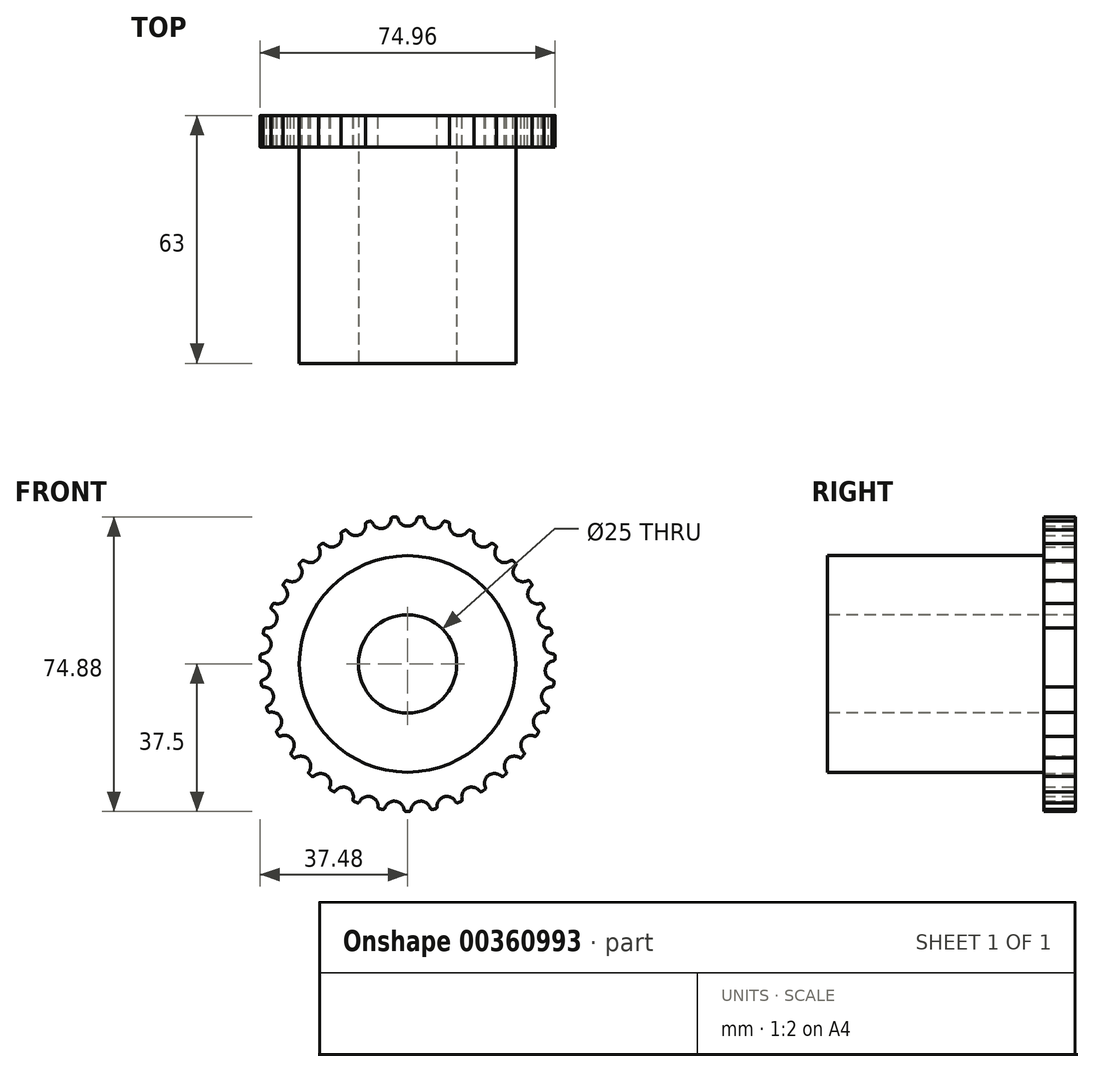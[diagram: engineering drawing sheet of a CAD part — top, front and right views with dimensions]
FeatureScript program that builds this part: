
annotation { "Feature Type Name" : "Feature", "Feature Type Description" : "" }
export const myFeature = defineFeature(function(context is Context, id is Id, definition is map)
    precondition{}
    {
        {
            var Q0;
            Q0=qCreatedBy(makeId("Front.planeOp"),FACE);
            var sketch = newSketch(context, id + "F0", { "sketchPlane" : qUnion([Q0])});
            skCircle(sketch, "E0", {"center": v(0, 0) * mm, "radius": 37.5 * mm});
            skSolve(sketch);
        }
        {
            var Q0;
            Q0=makeQuery(id+"F0.imprint","IMPRINT",FACE,{"disambiguationData":[TD([[makeQuery(id+"F0.imprint","IMPRINT",EDGE,{"derivedFrom":sQuery(id+"F0.wireOp",EDGE,"E0")}),1.0]])]});
            extrude(context, id + "F1", {"entities" : qUnion([Q0]), "endBound" : BoundingType.SYMMETRIC, "oppositeDirection" : true, "depth" : 8 * mm});
        }
        {
            var Q0;
            Q0=makeQuery(id+"F1.opExtrude","CAP_FACE",FACE,{"disambiguationData":[OSD([sQuery(id+"F0.wireOp",EDGE,"E0")])],"isStart":false});
            var sketch = newSketch(context, id + "F2", { "sketchPlane" : qUnion([Q0])});
            skArc(sketch, "E1", {"start": v(-2.45, 36.99) * mm, "mid": v(0, 35) * mm, "end": v(2.45, 36.99) * mm});
            skLineSegment(sketch, "E2", {"start": v(0, 0) * mm, "end": v(0, 37.5) * mm, "construction": true});
            skPoint(sketch, "E3.visualSharp", {"position": v(2.5, 37.42) * mm});
            skArc(sketch, "E3.filletArc", {"start": v(2.98, 37.38) * mm, "mid": v(2.64, 37.28) * mm, "end": v(2.45, 36.99) * mm});
            skPoint(sketch, "E4.visualSharp", {"position": v(-2.5, 37.42) * mm});
            skArc(sketch, "E4.filletArc", {"start": v(-2.45, 36.99) * mm, "mid": v(-2.64, 37.28) * mm, "end": v(-2.98, 37.38) * mm});
            skLineSegment(sketch, "E5", {"start": v(2.98, 37.38) * mm, "end": v(1.5, 39.5) * mm});
            skLineSegment(sketch, "E6", {"start": v(1.5, 39.5) * mm, "end": v(-1.5, 39.5) * mm});
            skLineSegment(sketch, "E7", {"start": v(-1.5, 39.5) * mm, "end": v(-2.98, 37.38) * mm});
            skLineSegment(sketch, "E8.1.0", {"start": v(-3.75, 37.31) * mm, "end": v(-5.58, 39.13) * mm});
            skLineSegment(sketch, "E8.1.1", {"start": v(-5.58, 39.13) * mm, "end": v(-8.53, 38.6) * mm});
            skLineSegment(sketch, "E8.1.2", {"start": v(-8.53, 38.6) * mm, "end": v(-9.6, 36.25) * mm});
            skArc(sketch, "E8.1.3", {"start": v(-9.01, 35.95) * mm, "mid": v(-9.25, 36.21) * mm, "end": v(-9.6, 36.25) * mm});
            skArc(sketch, "E8.1.4", {"start": v(-9.01, 35.95) * mm, "mid": v(-6.25, 34.44) * mm, "end": v(-4.2, 36.83) * mm});
            skArc(sketch, "E8.1.5", {"start": v(-3.75, 37.31) * mm, "mid": v(-4.06, 37.16) * mm, "end": v(-4.2, 36.83) * mm});
            skLineSegment(sketch, "E8.2.0", {"start": v(-10.35, 36.04) * mm, "end": v(-12.47, 37.5) * mm});
            skLineSegment(sketch, "E8.2.1", {"start": v(-12.47, 37.5) * mm, "end": v(-15.28, 36.45) * mm});
            skLineSegment(sketch, "E8.2.2", {"start": v(-15.28, 36.45) * mm, "end": v(-15.92, 33.95) * mm});
            skArc(sketch, "E8.2.3", {"start": v(-15.29, 33.77) * mm, "mid": v(-15.57, 33.98) * mm, "end": v(-15.92, 33.95) * mm});
            skArc(sketch, "E8.2.4", {"start": v(-15.29, 33.77) * mm, "mid": v(-12.3, 32.77) * mm, "end": v(-10.7, 35.49) * mm});
            skArc(sketch, "E8.2.5", {"start": v(-10.35, 36.04) * mm, "mid": v(-10.63, 35.83) * mm, "end": v(-10.7, 35.49) * mm});
            skLineSegment(sketch, "E8.3.0", {"start": v(-16.62, 33.62) * mm, "end": v(-18.97, 34.68) * mm});
            skLineSegment(sketch, "E8.3.1", {"start": v(-18.97, 34.68) * mm, "end": v(-21.55, 33.14) * mm});
            skLineSegment(sketch, "E8.3.2", {"start": v(-21.55, 33.14) * mm, "end": v(-21.73, 30.56) * mm});
            skArc(sketch, "E8.3.3", {"start": v(-21.07, 30.5) * mm, "mid": v(-21.39, 30.65) * mm, "end": v(-21.73, 30.56) * mm});
            skArc(sketch, "E8.3.4", {"start": v(-21.07, 30.5) * mm, "mid": v(-17.95, 30.05) * mm, "end": v(-16.87, 33) * mm});
            skArc(sketch, "E8.3.5", {"start": v(-16.62, 33.62) * mm, "mid": v(-16.86, 33.36) * mm, "end": v(-16.87, 33) * mm});
            skLineSegment(sketch, "E8.4.0", {"start": v(-22.35, 30.1) * mm, "end": v(-24.86, 30.73) * mm});
            skLineSegment(sketch, "E8.4.1", {"start": v(-24.86, 30.73) * mm, "end": v(-27.12, 28.76) * mm});
            skLineSegment(sketch, "E8.4.2", {"start": v(-27.12, 28.76) * mm, "end": v(-26.84, 26.2) * mm});
            skArc(sketch, "E8.4.3", {"start": v(-26.18, 26.24) * mm, "mid": v(-26.52, 26.34) * mm, "end": v(-26.84, 26.2) * mm});
            skArc(sketch, "E8.4.4", {"start": v(-26.18, 26.24) * mm, "mid": v(-23.03, 26.36) * mm, "end": v(-22.5, 29.46) * mm});
            skArc(sketch, "E8.4.5", {"start": v(-22.35, 30.1) * mm, "mid": v(-22.54, 29.81) * mm, "end": v(-22.5, 29.46) * mm});
            skLineSegment(sketch, "E8.5.0", {"start": v(-27.37, 25.63) * mm, "end": v(-29.95, 25.8) * mm});
            skLineSegment(sketch, "E8.5.1", {"start": v(-29.95, 25.8) * mm, "end": v(-31.82, 23.46) * mm});
            skLineSegment(sketch, "E8.5.2", {"start": v(-31.82, 23.46) * mm, "end": v(-31.08, 20.98) * mm});
            skArc(sketch, "E8.5.3", {"start": v(-30.44, 21.15) * mm, "mid": v(-30.8, 21.18) * mm, "end": v(-31.08, 20.98) * mm});
            skArc(sketch, "E8.5.4", {"start": v(-30.44, 21.15) * mm, "mid": v(-27.36, 21.82) * mm, "end": v(-27.4, 24.97) * mm});
            skArc(sketch, "E8.5.5", {"start": v(-27.37, 25.63) * mm, "mid": v(-27.5, 25.3) * mm, "end": v(-27.4, 24.97) * mm});
            skLineSegment(sketch, "E8.6.0", {"start": v(-31.5, 20.33) * mm, "end": v(-34.07, 20.04) * mm});
            skLineSegment(sketch, "E8.6.1", {"start": v(-34.07, 20.04) * mm, "end": v(-35.5, 17.4) * mm});
            skLineSegment(sketch, "E8.6.2", {"start": v(-35.5, 17.4) * mm, "end": v(-34.33, 15.1) * mm});
            skArc(sketch, "E8.6.3", {"start": v(-33.73, 15.37) * mm, "mid": v(-34.08, 15.35) * mm, "end": v(-34.33, 15.1) * mm});
            skArc(sketch, "E8.6.4", {"start": v(-33.73, 15.37) * mm, "mid": v(-30.82, 16.59) * mm, "end": v(-31.41, 19.68) * mm});
            skArc(sketch, "E8.6.5", {"start": v(-31.5, 20.33) * mm, "mid": v(-31.58, 19.99) * mm, "end": v(-31.41, 19.68) * mm});
            skLineSegment(sketch, "E8.7.0", {"start": v(-34.63, 14.38) * mm, "end": v(-37.1, 13.63) * mm});
            skLineSegment(sketch, "E8.7.1", {"start": v(-37.1, 13.63) * mm, "end": v(-38.03, 10.78) * mm});
            skLineSegment(sketch, "E8.7.2", {"start": v(-38.03, 10.78) * mm, "end": v(-36.47, 8.72) * mm});
            skArc(sketch, "E8.7.3", {"start": v(-35.93, 9.1) * mm, "mid": v(-36.27, 9.01) * mm, "end": v(-36.47, 8.72) * mm});
            skArc(sketch, "E8.7.4", {"start": v(-35.93, 9.1) * mm, "mid": v(-33.29, 10.82) * mm, "end": v(-34.42, 13.76) * mm});
            skArc(sketch, "E8.7.5", {"start": v(-34.63, 14.38) * mm, "mid": v(-34.64, 14.03) * mm, "end": v(-34.42, 13.76) * mm});
            skLineSegment(sketch, "E8.8.0", {"start": v(-36.64, 7.97) * mm, "end": v(-38.94, 6.79) * mm});
            skLineSegment(sketch, "E8.8.1", {"start": v(-38.94, 6.79) * mm, "end": v(-39.34, 3.82) * mm});
            skLineSegment(sketch, "E8.8.2", {"start": v(-39.34, 3.82) * mm, "end": v(-37.44, 2.07) * mm});
            skArc(sketch, "E8.8.3", {"start": v(-36.98, 2.54) * mm, "mid": v(-37.3, 2.4) * mm, "end": v(-37.44, 2.07) * mm});
            skArc(sketch, "E8.8.4", {"start": v(-36.98, 2.54) * mm, "mid": v(-34.68, 4.7) * mm, "end": v(-36.32, 7.39) * mm});
            skArc(sketch, "E8.8.5", {"start": v(-36.64, 7.97) * mm, "mid": v(-36.6, 7.62) * mm, "end": v(-36.32, 7.39) * mm});
            skLineSegment(sketch, "E8.9.0", {"start": v(-37.48, 1.3) * mm, "end": v(-39.53, -0.27) * mm});
            skLineSegment(sketch, "E8.9.1", {"start": v(-39.53, -0.27) * mm, "end": v(-39.4, -3.27) * mm});
            skLineSegment(sketch, "E8.9.2", {"start": v(-39.4, -3.27) * mm, "end": v(-37.21, -4.65) * mm});
            skArc(sketch, "E8.9.3", {"start": v(-36.84, -4.1) * mm, "mid": v(-37.13, -4.3) * mm, "end": v(-37.21, -4.65) * mm});
            skArc(sketch, "E8.9.4", {"start": v(-36.84, -4.1) * mm, "mid": v(-34.96, -1.57) * mm, "end": v(-37.06, 0.78) * mm});
            skArc(sketch, "E8.9.5", {"start": v(-37.48, 1.3) * mm, "mid": v(-37.36, 0.96) * mm, "end": v(-37.06, 0.78) * mm});
            skLineSegment(sketch, "E8.10.0", {"start": v(-37.1, -5.42) * mm, "end": v(-38.84, -7.33) * mm});
            skLineSegment(sketch, "E8.10.1", {"start": v(-38.84, -7.33) * mm, "end": v(-38.18, -10.25) * mm});
            skLineSegment(sketch, "E8.10.2", {"start": v(-38.18, -10.25) * mm, "end": v(-35.78, -11.22) * mm});
            skArc(sketch, "E8.10.3", {"start": v(-35.51, -10.62) * mm, "mid": v(-35.76, -10.87) * mm, "end": v(-35.78, -11.22) * mm});
            skArc(sketch, "E8.10.4", {"start": v(-35.51, -10.62) * mm, "mid": v(-34.12, -7.79) * mm, "end": v(-36.6, -5.84) * mm});
            skArc(sketch, "E8.10.5", {"start": v(-37.1, -5.42) * mm, "mid": v(-36.94, -5.73) * mm, "end": v(-36.6, -5.84) * mm});
            skLineSegment(sketch, "E8.11.0", {"start": v(-35.54, -11.96) * mm, "end": v(-36.91, -14.15) * mm});
            skLineSegment(sketch, "E8.11.1", {"start": v(-36.91, -14.15) * mm, "end": v(-35.73, -16.9) * mm});
            skLineSegment(sketch, "E8.11.2", {"start": v(-35.73, -16.9) * mm, "end": v(-33.2, -17.43) * mm});
            skArc(sketch, "E8.11.3", {"start": v(-33.05, -16.79) * mm, "mid": v(-33.25, -17.08) * mm, "end": v(-33.2, -17.43) * mm});
            skArc(sketch, "E8.11.4", {"start": v(-33.05, -16.79) * mm, "mid": v(-32.18, -13.76) * mm, "end": v(-34.97, -12.29) * mm});
            skArc(sketch, "E8.11.5", {"start": v(-35.54, -11.96) * mm, "mid": v(-35.32, -12.23) * mm, "end": v(-34.97, -12.29) * mm});
            skLineSegment(sketch, "E8.12.0", {"start": v(-32.84, -18.11) * mm, "end": v(-33.8, -20.5) * mm});
            skLineSegment(sketch, "E8.12.1", {"start": v(-33.8, -20.5) * mm, "end": v(-32.14, -23.01) * mm});
            skLineSegment(sketch, "E8.12.2", {"start": v(-32.14, -23.01) * mm, "end": v(-29.56, -23.08) * mm});
            skArc(sketch, "E8.12.3", {"start": v(-29.52, -22.42) * mm, "mid": v(-29.66, -22.74) * mm, "end": v(-29.56, -23.08) * mm});
            skArc(sketch, "E8.12.4", {"start": v(-29.52, -22.42) * mm, "mid": v(-29.21, -19.28) * mm, "end": v(-32.22, -18.33) * mm});
            skArc(sketch, "E8.12.5", {"start": v(-32.84, -18.11) * mm, "mid": v(-32.57, -18.34) * mm, "end": v(-32.22, -18.33) * mm});
            skLineSegment(sketch, "E8.13.0", {"start": v(-29.08, -23.68) * mm, "end": v(-29.59, -26.21) * mm});
            skLineSegment(sketch, "E8.13.1", {"start": v(-29.59, -26.21) * mm, "end": v(-27.51, -28.38) * mm});
            skLineSegment(sketch, "E8.13.2", {"start": v(-27.51, -28.38) * mm, "end": v(-24.96, -27.98) * mm});
            skArc(sketch, "E8.13.3", {"start": v(-25.04, -27.33) * mm, "mid": v(-25.13, -27.67) * mm, "end": v(-24.96, -27.98) * mm});
            skArc(sketch, "E8.13.4", {"start": v(-25.04, -27.33) * mm, "mid": v(-25.3, -24.19) * mm, "end": v(-28.42, -23.8) * mm});
            skArc(sketch, "E8.13.5", {"start": v(-29.08, -23.68) * mm, "mid": v(-28.77, -23.86) * mm, "end": v(-28.42, -23.8) * mm});
            skLineSegment(sketch, "E8.14.0", {"start": v(-24.38, -28.5) * mm, "end": v(-24.43, -31.07) * mm});
            skLineSegment(sketch, "E8.14.1", {"start": v(-24.43, -31.07) * mm, "end": v(-22, -32.84) * mm});
            skLineSegment(sketch, "E8.14.2", {"start": v(-22, -32.84) * mm, "end": v(-19.57, -32) * mm});
            skArc(sketch, "E8.14.3", {"start": v(-19.76, -31.36) * mm, "mid": v(-19.78, -31.71) * mm, "end": v(-19.57, -32) * mm});
            skArc(sketch, "E8.14.4", {"start": v(-19.76, -31.36) * mm, "mid": v(-20.57, -28.32) * mm, "end": v(-23.72, -28.48) * mm});
            skArc(sketch, "E8.14.5", {"start": v(-24.38, -28.5) * mm, "mid": v(-24.05, -28.61) * mm, "end": v(-23.72, -28.48) * mm});
            skLineSegment(sketch, "E8.15.0", {"start": v(-18.9, -32.39) * mm, "end": v(-18.49, -34.94) * mm});
            skLineSegment(sketch, "E8.15.1", {"start": v(-18.49, -34.94) * mm, "end": v(-15.79, -36.24) * mm});
            skLineSegment(sketch, "E8.15.2", {"start": v(-15.79, -36.24) * mm, "end": v(-13.54, -34.97) * mm});
            skArc(sketch, "E8.15.3", {"start": v(-13.84, -34.38) * mm, "mid": v(-13.8, -34.74) * mm, "end": v(-13.54, -34.97) * mm});
            skArc(sketch, "E8.15.4", {"start": v(-13.84, -34.38) * mm, "mid": v(-15.19, -31.53) * mm, "end": v(-18.25, -32.26) * mm});
            skArc(sketch, "E8.15.5", {"start": v(-18.9, -32.39) * mm, "mid": v(-18.55, -32.45) * mm, "end": v(-18.25, -32.26) * mm});
            skLineSegment(sketch, "E8.16.0", {"start": v(-12.81, -35.24) * mm, "end": v(-11.95, -37.68) * mm});
            skLineSegment(sketch, "E8.16.1", {"start": v(-11.95, -37.68) * mm, "end": v(-9.06, -38.48) * mm});
            skLineSegment(sketch, "E8.16.2", {"start": v(-9.06, -38.48) * mm, "end": v(-7.08, -36.83) * mm});
            skArc(sketch, "E8.16.3", {"start": v(-7.48, -36.3) * mm, "mid": v(-7.38, -36.64) * mm, "end": v(-7.08, -36.83) * mm});
            skArc(sketch, "E8.16.4", {"start": v(-7.48, -36.3) * mm, "mid": v(-9.31, -33.74) * mm, "end": v(-12.2, -35) * mm});
            skArc(sketch, "E8.16.5", {"start": v(-12.81, -35.24) * mm, "mid": v(-12.46, -35.24) * mm, "end": v(-12.2, -35) * mm});
            skLineSegment(sketch, "E8.17.0", {"start": v(-6.31, -36.96) * mm, "end": v(-5.03, -39.2) * mm});
            skLineSegment(sketch, "E8.17.1", {"start": v(-5.03, -39.2) * mm, "end": v(-2.05, -39.48) * mm});
            skLineSegment(sketch, "E8.17.2", {"start": v(-2.05, -39.48) * mm, "end": v(-0.39, -37.5) * mm});
            skArc(sketch, "E8.17.3", {"start": v(-0.88, -37.06) * mm, "mid": v(-0.72, -37.37) * mm, "end": v(-0.39, -37.5) * mm});
            skArc(sketch, "E8.17.4", {"start": v(-0.88, -37.06) * mm, "mid": v(-3.14, -34.86) * mm, "end": v(-5.75, -36.62) * mm});
            skArc(sketch, "E8.17.5", {"start": v(-6.31, -36.96) * mm, "mid": v(-5.97, -36.9) * mm, "end": v(-5.75, -36.62) * mm});
            skLineSegment(sketch, "E8.18.0", {"start": v(0.39, -37.5) * mm, "end": v(2.05, -39.48) * mm});
            skLineSegment(sketch, "E8.18.1", {"start": v(2.05, -39.48) * mm, "end": v(5.03, -39.2) * mm});
            skLineSegment(sketch, "E8.18.2", {"start": v(5.03, -39.2) * mm, "end": v(6.31, -36.96) * mm});
            skArc(sketch, "E8.18.3", {"start": v(5.75, -36.62) * mm, "mid": v(5.97, -36.9) * mm, "end": v(6.31, -36.96) * mm});
            skArc(sketch, "E8.18.4", {"start": v(5.75, -36.62) * mm, "mid": v(3.14, -34.86) * mm, "end": v(0.88, -37.06) * mm});
            skArc(sketch, "E8.18.5", {"start": v(0.39, -37.5) * mm, "mid": v(0.72, -37.37) * mm, "end": v(0.88, -37.06) * mm});
            skLineSegment(sketch, "E8.19.0", {"start": v(7.08, -36.83) * mm, "end": v(9.06, -38.48) * mm});
            skLineSegment(sketch, "E8.19.1", {"start": v(9.06, -38.48) * mm, "end": v(11.95, -37.68) * mm});
            skLineSegment(sketch, "E8.19.2", {"start": v(11.95, -37.68) * mm, "end": v(12.81, -35.24) * mm});
            skArc(sketch, "E8.19.3", {"start": v(12.2, -35) * mm, "mid": v(12.46, -35.24) * mm, "end": v(12.81, -35.24) * mm});
            skArc(sketch, "E8.19.4", {"start": v(12.2, -35) * mm, "mid": v(9.31, -33.74) * mm, "end": v(7.48, -36.3) * mm});
            skArc(sketch, "E8.19.5", {"start": v(7.08, -36.83) * mm, "mid": v(7.38, -36.64) * mm, "end": v(7.48, -36.3) * mm});
            skLineSegment(sketch, "E8.20.0", {"start": v(13.54, -34.97) * mm, "end": v(15.79, -36.24) * mm});
            skLineSegment(sketch, "E8.20.1", {"start": v(15.79, -36.24) * mm, "end": v(18.49, -34.94) * mm});
            skLineSegment(sketch, "E8.20.2", {"start": v(18.49, -34.94) * mm, "end": v(18.9, -32.39) * mm});
            skArc(sketch, "E8.20.3", {"start": v(18.25, -32.26) * mm, "mid": v(18.55, -32.45) * mm, "end": v(18.9, -32.39) * mm});
            skArc(sketch, "E8.20.4", {"start": v(18.25, -32.26) * mm, "mid": v(15.19, -31.53) * mm, "end": v(13.84, -34.38) * mm});
            skArc(sketch, "E8.20.5", {"start": v(13.54, -34.97) * mm, "mid": v(13.8, -34.74) * mm, "end": v(13.84, -34.38) * mm});
            skLineSegment(sketch, "E8.21.0", {"start": v(19.57, -32) * mm, "end": v(22, -32.84) * mm});
            skLineSegment(sketch, "E8.21.1", {"start": v(22, -32.84) * mm, "end": v(24.43, -31.07) * mm});
            skLineSegment(sketch, "E8.21.2", {"start": v(24.43, -31.07) * mm, "end": v(24.38, -28.5) * mm});
            skArc(sketch, "E8.21.3", {"start": v(23.72, -28.48) * mm, "mid": v(24.05, -28.61) * mm, "end": v(24.38, -28.5) * mm});
            skArc(sketch, "E8.21.4", {"start": v(23.72, -28.48) * mm, "mid": v(20.57, -28.32) * mm, "end": v(19.76, -31.36) * mm});
            skArc(sketch, "E8.21.5", {"start": v(19.57, -32) * mm, "mid": v(19.78, -31.71) * mm, "end": v(19.76, -31.36) * mm});
            skLineSegment(sketch, "E8.22.0", {"start": v(24.96, -27.98) * mm, "end": v(27.51, -28.38) * mm});
            skLineSegment(sketch, "E8.22.1", {"start": v(27.51, -28.38) * mm, "end": v(29.59, -26.21) * mm});
            skLineSegment(sketch, "E8.22.2", {"start": v(29.59, -26.21) * mm, "end": v(29.08, -23.68) * mm});
            skArc(sketch, "E8.22.3", {"start": v(28.42, -23.8) * mm, "mid": v(28.77, -23.86) * mm, "end": v(29.08, -23.68) * mm});
            skArc(sketch, "E8.22.4", {"start": v(28.42, -23.8) * mm, "mid": v(25.3, -24.19) * mm, "end": v(25.04, -27.33) * mm});
            skArc(sketch, "E8.22.5", {"start": v(24.96, -27.98) * mm, "mid": v(25.13, -27.67) * mm, "end": v(25.04, -27.33) * mm});
            skLineSegment(sketch, "E8.23.0", {"start": v(29.56, -23.08) * mm, "end": v(32.14, -23.01) * mm});
            skLineSegment(sketch, "E8.23.1", {"start": v(32.14, -23.01) * mm, "end": v(33.8, -20.5) * mm});
            skLineSegment(sketch, "E8.23.2", {"start": v(33.8, -20.5) * mm, "end": v(32.84, -18.11) * mm});
            skArc(sketch, "E8.23.3", {"start": v(32.22, -18.33) * mm, "mid": v(32.57, -18.34) * mm, "end": v(32.84, -18.11) * mm});
            skArc(sketch, "E8.23.4", {"start": v(32.22, -18.33) * mm, "mid": v(29.21, -19.28) * mm, "end": v(29.52, -22.42) * mm});
            skArc(sketch, "E8.23.5", {"start": v(29.56, -23.08) * mm, "mid": v(29.66, -22.74) * mm, "end": v(29.52, -22.42) * mm});
            skLineSegment(sketch, "E8.24.0", {"start": v(33.2, -17.43) * mm, "end": v(35.73, -16.9) * mm});
            skLineSegment(sketch, "E8.24.1", {"start": v(35.73, -16.9) * mm, "end": v(36.91, -14.15) * mm});
            skLineSegment(sketch, "E8.24.2", {"start": v(36.91, -14.15) * mm, "end": v(35.54, -11.96) * mm});
            skArc(sketch, "E8.24.3", {"start": v(34.97, -12.29) * mm, "mid": v(35.32, -12.23) * mm, "end": v(35.54, -11.96) * mm});
            skArc(sketch, "E8.24.4", {"start": v(34.97, -12.29) * mm, "mid": v(32.18, -13.76) * mm, "end": v(33.05, -16.79) * mm});
            skArc(sketch, "E8.24.5", {"start": v(33.2, -17.43) * mm, "mid": v(33.25, -17.08) * mm, "end": v(33.05, -16.79) * mm});
            skLineSegment(sketch, "E8.25.0", {"start": v(35.78, -11.22) * mm, "end": v(38.18, -10.25) * mm});
            skLineSegment(sketch, "E8.25.1", {"start": v(38.18, -10.25) * mm, "end": v(38.84, -7.33) * mm});
            skLineSegment(sketch, "E8.25.2", {"start": v(38.84, -7.33) * mm, "end": v(37.1, -5.42) * mm});
            skArc(sketch, "E8.25.3", {"start": v(36.6, -5.84) * mm, "mid": v(36.94, -5.73) * mm, "end": v(37.1, -5.42) * mm});
            skArc(sketch, "E8.25.4", {"start": v(36.6, -5.84) * mm, "mid": v(34.12, -7.79) * mm, "end": v(35.51, -10.62) * mm});
            skArc(sketch, "E8.25.5", {"start": v(35.78, -11.22) * mm, "mid": v(35.76, -10.87) * mm, "end": v(35.51, -10.62) * mm});
            skLineSegment(sketch, "E8.26.0", {"start": v(37.21, -4.65) * mm, "end": v(39.4, -3.27) * mm});
            skLineSegment(sketch, "E8.26.1", {"start": v(39.4, -3.27) * mm, "end": v(39.53, -0.27) * mm});
            skLineSegment(sketch, "E8.26.2", {"start": v(39.53, -0.27) * mm, "end": v(37.48, 1.3) * mm});
            skArc(sketch, "E8.26.3", {"start": v(37.06, 0.78) * mm, "mid": v(37.36, 0.96) * mm, "end": v(37.48, 1.3) * mm});
            skArc(sketch, "E8.26.4", {"start": v(37.06, 0.78) * mm, "mid": v(34.96, -1.57) * mm, "end": v(36.84, -4.1) * mm});
            skArc(sketch, "E8.26.5", {"start": v(37.21, -4.65) * mm, "mid": v(37.13, -4.3) * mm, "end": v(36.84, -4.1) * mm});
            skLineSegment(sketch, "E8.27.0", {"start": v(37.44, 2.07) * mm, "end": v(39.34, 3.82) * mm});
            skLineSegment(sketch, "E8.27.1", {"start": v(39.34, 3.82) * mm, "end": v(38.94, 6.79) * mm});
            skLineSegment(sketch, "E8.27.2", {"start": v(38.94, 6.79) * mm, "end": v(36.64, 7.97) * mm});
            skArc(sketch, "E8.27.3", {"start": v(36.32, 7.39) * mm, "mid": v(36.6, 7.62) * mm, "end": v(36.64, 7.97) * mm});
            skArc(sketch, "E8.27.4", {"start": v(36.32, 7.39) * mm, "mid": v(34.68, 4.7) * mm, "end": v(36.98, 2.54) * mm});
            skArc(sketch, "E8.27.5", {"start": v(37.44, 2.07) * mm, "mid": v(37.3, 2.4) * mm, "end": v(36.98, 2.54) * mm});
            skLineSegment(sketch, "E8.28.0", {"start": v(36.47, 8.72) * mm, "end": v(38.03, 10.78) * mm});
            skLineSegment(sketch, "E8.28.1", {"start": v(38.03, 10.78) * mm, "end": v(37.1, 13.63) * mm});
            skLineSegment(sketch, "E8.28.2", {"start": v(37.1, 13.63) * mm, "end": v(34.63, 14.38) * mm});
            skArc(sketch, "E8.28.3", {"start": v(34.42, 13.76) * mm, "mid": v(34.64, 14.03) * mm, "end": v(34.63, 14.38) * mm});
            skArc(sketch, "E8.28.4", {"start": v(34.42, 13.76) * mm, "mid": v(33.29, 10.82) * mm, "end": v(35.93, 9.1) * mm});
            skArc(sketch, "E8.28.5", {"start": v(36.47, 8.72) * mm, "mid": v(36.27, 9.01) * mm, "end": v(35.93, 9.1) * mm});
            skLineSegment(sketch, "E8.29.0", {"start": v(34.33, 15.1) * mm, "end": v(35.5, 17.4) * mm});
            skLineSegment(sketch, "E8.29.1", {"start": v(35.5, 17.4) * mm, "end": v(34.07, 20.04) * mm});
            skLineSegment(sketch, "E8.29.2", {"start": v(34.07, 20.04) * mm, "end": v(31.5, 20.33) * mm});
            skArc(sketch, "E8.29.3", {"start": v(31.41, 19.68) * mm, "mid": v(31.58, 19.99) * mm, "end": v(31.5, 20.33) * mm});
            skArc(sketch, "E8.29.4", {"start": v(31.41, 19.68) * mm, "mid": v(30.82, 16.59) * mm, "end": v(33.73, 15.37) * mm});
            skArc(sketch, "E8.29.5", {"start": v(34.33, 15.1) * mm, "mid": v(34.08, 15.35) * mm, "end": v(33.73, 15.37) * mm});
            skLineSegment(sketch, "E8.30.0", {"start": v(31.08, 20.98) * mm, "end": v(31.82, 23.46) * mm});
            skLineSegment(sketch, "E8.30.1", {"start": v(31.82, 23.46) * mm, "end": v(29.95, 25.8) * mm});
            skLineSegment(sketch, "E8.30.2", {"start": v(29.95, 25.8) * mm, "end": v(27.37, 25.63) * mm});
            skArc(sketch, "E8.30.3", {"start": v(27.4, 24.97) * mm, "mid": v(27.5, 25.3) * mm, "end": v(27.37, 25.63) * mm});
            skArc(sketch, "E8.30.4", {"start": v(27.4, 24.97) * mm, "mid": v(27.36, 21.82) * mm, "end": v(30.44, 21.15) * mm});
            skArc(sketch, "E8.30.5", {"start": v(31.08, 20.98) * mm, "mid": v(30.8, 21.18) * mm, "end": v(30.44, 21.15) * mm});
            skLineSegment(sketch, "E8.31.0", {"start": v(26.84, 26.2) * mm, "end": v(27.12, 28.76) * mm});
            skLineSegment(sketch, "E8.31.1", {"start": v(27.12, 28.76) * mm, "end": v(24.86, 30.73) * mm});
            skLineSegment(sketch, "E8.31.2", {"start": v(24.86, 30.73) * mm, "end": v(22.35, 30.1) * mm});
            skArc(sketch, "E8.31.3", {"start": v(22.5, 29.46) * mm, "mid": v(22.54, 29.81) * mm, "end": v(22.35, 30.1) * mm});
            skArc(sketch, "E8.31.4", {"start": v(22.5, 29.46) * mm, "mid": v(23.03, 26.36) * mm, "end": v(26.18, 26.24) * mm});
            skArc(sketch, "E8.31.5", {"start": v(26.84, 26.2) * mm, "mid": v(26.52, 26.34) * mm, "end": v(26.18, 26.24) * mm});
            skLineSegment(sketch, "E8.32.0", {"start": v(21.73, 30.56) * mm, "end": v(21.55, 33.14) * mm});
            skLineSegment(sketch, "E8.32.1", {"start": v(21.55, 33.14) * mm, "end": v(18.97, 34.68) * mm});
            skLineSegment(sketch, "E8.32.2", {"start": v(18.97, 34.68) * mm, "end": v(16.62, 33.62) * mm});
            skArc(sketch, "E8.32.3", {"start": v(16.87, 33) * mm, "mid": v(16.86, 33.36) * mm, "end": v(16.62, 33.62) * mm});
            skArc(sketch, "E8.32.4", {"start": v(16.87, 33) * mm, "mid": v(17.95, 30.05) * mm, "end": v(21.07, 30.5) * mm});
            skArc(sketch, "E8.32.5", {"start": v(21.73, 30.56) * mm, "mid": v(21.39, 30.65) * mm, "end": v(21.07, 30.5) * mm});
            skLineSegment(sketch, "E8.33.0", {"start": v(15.92, 33.95) * mm, "end": v(15.28, 36.45) * mm});
            skLineSegment(sketch, "E8.33.1", {"start": v(15.28, 36.45) * mm, "end": v(12.47, 37.5) * mm});
            skLineSegment(sketch, "E8.33.2", {"start": v(12.47, 37.5) * mm, "end": v(10.35, 36.04) * mm});
            skArc(sketch, "E8.33.3", {"start": v(10.7, 35.49) * mm, "mid": v(10.63, 35.83) * mm, "end": v(10.35, 36.04) * mm});
            skArc(sketch, "E8.33.4", {"start": v(10.7, 35.49) * mm, "mid": v(12.3, 32.77) * mm, "end": v(15.29, 33.77) * mm});
            skArc(sketch, "E8.33.5", {"start": v(15.92, 33.95) * mm, "mid": v(15.57, 33.98) * mm, "end": v(15.29, 33.77) * mm});
            skLineSegment(sketch, "E8.34.0", {"start": v(9.6, 36.25) * mm, "end": v(8.53, 38.6) * mm});
            skLineSegment(sketch, "E8.34.1", {"start": v(8.53, 38.6) * mm, "end": v(5.58, 39.13) * mm});
            skLineSegment(sketch, "E8.34.2", {"start": v(5.58, 39.13) * mm, "end": v(3.75, 37.31) * mm});
            skArc(sketch, "E8.34.3", {"start": v(4.2, 36.83) * mm, "mid": v(4.06, 37.16) * mm, "end": v(3.75, 37.31) * mm});
            skArc(sketch, "E8.34.4", {"start": v(4.2, 36.83) * mm, "mid": v(6.25, 34.44) * mm, "end": v(9.01, 35.95) * mm});
            skArc(sketch, "E8.34.5", {"start": v(9.6, 36.25) * mm, "mid": v(9.25, 36.21) * mm, "end": v(9.01, 35.95) * mm});
            skPoint(sketch, "E8.center", {"position": v(0, 0) * mm});
            skSolve(sketch);
        }
        {
            var Q0;
            Q0 = qSketchRegion(id + "F2", true);
            extrude(context, id + "F3", {"entities" : qUnion([Q0]), "operationType" : NewBodyOperationType.REMOVE, "endBound" : BoundingType.THROUGH_ALL, "oppositeDirection" : true, "depth" : 25 * mm});
        }
        {
            var Q0;
            Q0=makeQuery(id+"F1.opExtrude","CAP_FACE",FACE,{"disambiguationData":[OSD([sQuery(id+"F0.wireOp",EDGE,"E0")])],"isStart":true});
            var sketch = newSketch(context, id + "F4", { "sketchPlane" : qUnion([Q0])});
            skCircle(sketch, "E9", {"center": v(0, 0) * mm, "radius": 27.5 * mm});
            skSolve(sketch);
        }
        {
            var Q0;
            Q0 = qSketchRegion(id + "F4", true);
            extrude(context, id + "F5", {"entities" : qUnion([Q0]), "operationType" : NewBodyOperationType.ADD, "depth" : 55 * mm});
        }
        {
            var Q0;
            Q0=makeQuery(id+"F5.opExtrude","CAP_FACE",FACE,{"disambiguationData":[OSD([sQuery(id+"F4.wireOp",EDGE,"E9")])],"isStart":false});
            var sketch = newSketch(context, id + "F6", { "sketchPlane" : qUnion([Q0])});
            skCircle(sketch, "E10", {"center": v(0, 0) * mm, "radius": 12.5 * mm});
            skSolve(sketch);
        }
        {
            var Q0;
            Q0 = qSketchRegion(id + "F6", true);
            extrude(context, id + "F7", {"entities" : qUnion([Q0]), "operationType" : NewBodyOperationType.REMOVE, "endBound" : BoundingType.THROUGH_ALL, "oppositeDirection" : true, "depth" : 118.42 * mm});
        }
    });
